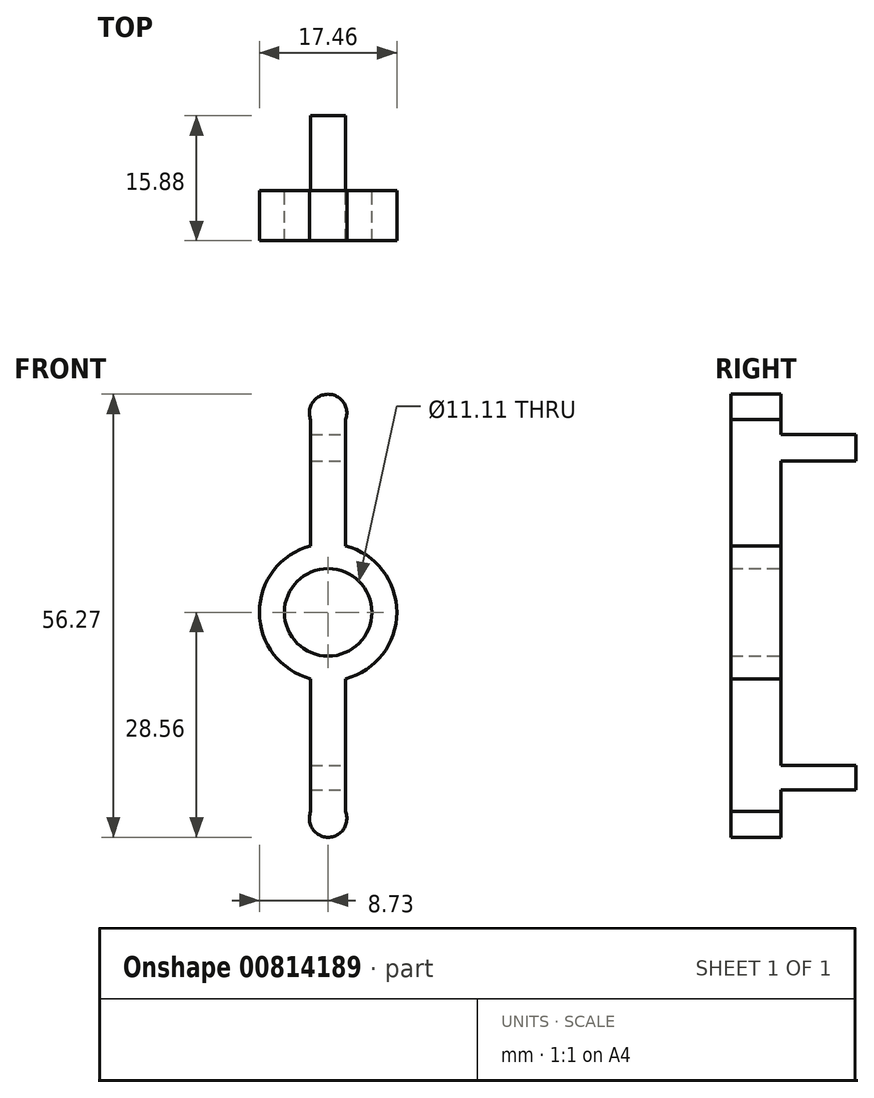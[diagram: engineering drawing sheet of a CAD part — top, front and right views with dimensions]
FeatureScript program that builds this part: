
annotation { "Feature Type Name" : "Feature", "Feature Type Description" : "" }
export const myFeature = defineFeature(function(context is Context, id is Id, definition is map)
    precondition{}
    {
        {
            var Q0;
            Q0=qCreatedBy(makeId("Front.planeOp"),FACE);
            var sketch = newSketch(context, id + "F0", { "sketchPlane" : qUnion([Q0])});
            skPoint(sketch, "E0.middle", {"position": v(0, 0) * mm});
            skCircle(sketch, "E1", {"center": v(0, 0) * mm, "radius": 5.56 * mm});
            skCircle(sketch, "E2", {"center": v(0, 0) * mm, "radius": 8.73 * mm});
            skCircle(sketch, "E3", {"center": v(0, -26.18) * mm, "radius": 2.38 * mm});
            skLineSegment(sketch, "E4", {"start": v(-2.22, -8.45) * mm, "end": v(-2.22, -25.31) * mm});
            skLineSegment(sketch, "E5", {"start": v(2.22, -8.45) * mm, "end": v(2.22, -25.31) * mm});
            skLineSegment(sketch, "E6", {"start": v(-2.22, 8.45) * mm, "end": v(-2.22, 24.44) * mm});
            skLineSegment(sketch, "E7", {"start": v(2.22, 8.45) * mm, "end": v(2.22, 24.47) * mm});
            skCircle(sketch, "E8", {"center": v(0, 25.33) * mm, "radius": 2.38 * mm});
            skPoint(sketch, "E8.third.point", {"position": v(0, 27.7) * mm});
            skPoint(sketch, "E9.endSnap0", {"position": v(2.22, 16.46) * mm});
            skLineSegment(sketch, "E10", {"start": v(2.22, 12.14) * mm, "end": v(2.22, 12.14) * mm});
            skLineSegment(sketch, "E11", {"start": v(-2.22, 22.57) * mm, "end": v(2.22, 22.57) * mm});
            skLineSegment(sketch, "E12", {"start": v(-2.22, 19.24) * mm, "end": v(2.22, 19.24) * mm});
            skLineSegment(sketch, "E13", {"start": v(-2.22, -19.42) * mm, "end": v(2.22, -19.42) * mm});
            skLineSegment(sketch, "E14", {"start": v(-2.22, -22.57) * mm, "end": v(2.22, -22.57) * mm});
            skSolve(sketch);
        }
        {
            var Q0;
            Q0=makeQuery(id+"F0.imprint","IMPRINT",FACE,{"disambiguationData":[TD([[makeQuery(id+"F0.imprint","IMPRINT",EDGE,{"derivedFrom":sQuery(id+"F0.wireOp",EDGE,"E1")}),-1.0]])]});
            var Q1;
            {var subQ0=sQuery(id+"F0.wireOp",EDGE,"E6");Q1=makeQuery(id+"F0.imprint","IMPRINT",FACE,{"disambiguationData":[TD([[makeQuery(id+"F0.imprint","IMPRINT",EDGE,{"derivedFrom":subQ0}),-1.0]])]});}
            var Q2;
            {var subQ0=sQuery(id+"F0.wireOp",EDGE,"E8");var subQ1=makeQuery(id+"F0.imprint","INTERSECT",VERTEX,{"derivedFrom":[sQuery(id+"F0.wireOp",EDGE,"E6"),subQ0]});Q2=makeQuery(id+"F0.imprint","IMPRINT",FACE,{"disambiguationData":[TD([[makeQuery(id+"F0.imprint","IMPRINT",EDGE,{"disambiguationData":[TD([[subQ1,-1.0]])],"derivedFrom":subQ0}),1.0]])]});}
            var Q3;
            {var subQ0=sQuery(id+"F0.wireOp",EDGE,"E3");var subQ1=makeQuery(id+"F0.imprint","INTERSECT",VERTEX,{"derivedFrom":[subQ0,sQuery(id+"F0.wireOp",EDGE,"E4")]});Q3=makeQuery(id+"F0.imprint","IMPRINT",FACE,{"disambiguationData":[TD([[makeQuery(id+"F0.imprint","IMPRINT",EDGE,{"disambiguationData":[TD([[subQ1,1.0]])],"derivedFrom":subQ0}),1.0]])]});}
            var Q4;
            {var subQ6=sQuery(id+"F0.wireOp",EDGE,"E5");Q4=makeQuery(id+"F0.imprint","IMPRINT",FACE,{"disambiguationData":[TD([[makeQuery(id+"F0.imprint","IMPRINT",EDGE,{"derivedFrom":subQ6}),-1.0]])]});}
            extrude(context, id + "F1", {"entities" : qUnion([Q0, Q1, Q2, Q3, Q4]), "depth" : 6.35 * mm, "offsetDistance" : 25.4 * mm});
        }
        {
            var Q0;
            {var subQ0=sQuery(id+"F0.wireOp",EDGE,"E11");Q0=makeQuery(id+"F0.imprint","IMPRINT",FACE,{"disambiguationData":[TD([[makeQuery(id+"F0.imprint","IMPRINT",EDGE,{"derivedFrom":subQ0}),-1.0]])]});}
            var Q1;
            {var subQ0=sQuery(id+"F0.wireOp",EDGE,"E13");Q1=makeQuery(id+"F0.imprint","IMPRINT",FACE,{"disambiguationData":[TD([[makeQuery(id+"F0.imprint","IMPRINT",EDGE,{"derivedFrom":subQ0}),-1.0]])]});}
            extrude(context, id + "F2", {"entities" : qUnion([Q0, Q1]), "operationType" : NewBodyOperationType.ADD, "depth" : -9.52 * mm, "offsetDistance" : 25.4 * mm});
        }
    });
